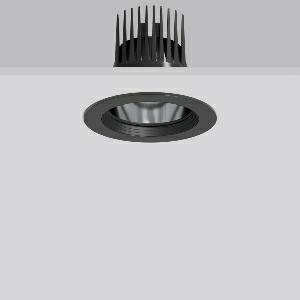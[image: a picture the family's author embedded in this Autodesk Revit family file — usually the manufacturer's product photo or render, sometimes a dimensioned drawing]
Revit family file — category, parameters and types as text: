
# Revit family: heledon_maxi_e_901784_003_2_76_8aa7
name_source: partatom
category: Lighting Fixtures
units: mm (PartAtom-declared; Revit-internal decimal feet)

## family parameters
Cut with Voids When Loaded = No
Host = Face
Light Source = No
Part Type = Normal
Room Calculation Point = No
Round Connector Dimension = Use Diameter
Shared = No

## types (1)
- HELEDON maxi E (1 x LED Modul 927 bakery, 3300 lm, 2700)
    Apparent Load = 33 VA
    Approval mark = CE
    CIE Flux Codes = 100 100 100 100 100
    Color Rendering = 90
    Color Temperature = 2700
    Default Elevation = 1800 mm
    Description = Series: HELEDON maxi
Round recessed downlight. Housing: die-cast aluminium, powder-coated. Black plastic ring and recessed LED to prevent glare from the side. Optical assembly with reflector made of MIRO-Silver with 98% total light reflection for outstanding efficiency - can be changed without tools. Special LED for illumination of pastries included. Suitable for Recessed ceiling mounting. Installation without tools thanks to spring fastening system. Including separate LED converter with connecting cable 600 mm.High quality converter without flickering and stroboscopic effect. Through-wiring box (5 pole) available as accessory. The following accessories can be mounted without use of tools: interchangeable lenses, decorative glasses, honeycomb louvre, clear and frosted diffusers, white interchangeable plastic ring. 
Colour: deep black, matt (RAL 9005)
Diameter: 162 mm
Height: 3 mm
Cut-out diameter: 152 mm
Recess height: 200 mm
Luminaire: recess height: 135 mm
Lamp: LED
Socket: without socket
Colour temperature: bakery
Colour rendering index (CRI): 97
System power: 33 W
Rated luminous flux: 3300 lm
Luminous efficiency: 100 lm/W
Control gear: Converter, dimmable, DALI
Protection class: II
Type of protection: IP 20
    Height = 0 mm  [stored 0 ft]
    Lamp = 1 x LED Modul 927 bakery
    Lamp Light Flux = 3300 lm
    Lamp count = 1
    Length = 162 mm
    Lifetime = 50000 h
    Luminous efficacy = 100 lm/W
    Manufacturer = RZB
    ModVariant = No
    Model = 901784.003.2.76
    Mounting Place = Ceiling
    Mounting Type = Recessed
    Number of Poles = 1
    OnlyDefault = Yes
    Power Factor = 1
    Product Name = HELEDON maxi E
    Product group = Recessed downlights
    ProductGroupID = 402
    Protection Class = Protection class II
    Protection Degree = IP 20
    RLX_Detail_Level = 1
    RLX_Emergency_Light_Flux = 0 lm
    RLX_Emergency_Type = 0
    RLX_Emergency_Type_DB = No
    RlxData = <blob elided: 122677 chars, md5=76bf18cc>
    Socket = socket
    Standby Power = 0 W
    System Light Flux = 3300 lm
    System Power = 33 W
    Type Comments = Product without accessories
    Type Image = 901662.003.jpg
    URL = http://relux.com
    VarID = ---
    Voltage = 230 V
    Voltage Range = 220-240 V
    Weight = 0.00 kg
    Width = 0 mm  [stored 0 ft]

note: [stored X ft] marks values corroborated as IEEE doubles in the binary element streams (Revit-internal decimal feet)

## geometry (parser evidence)
native form markers: Blend x4, Sweep x13
no freeform markers — native parametric forms only
